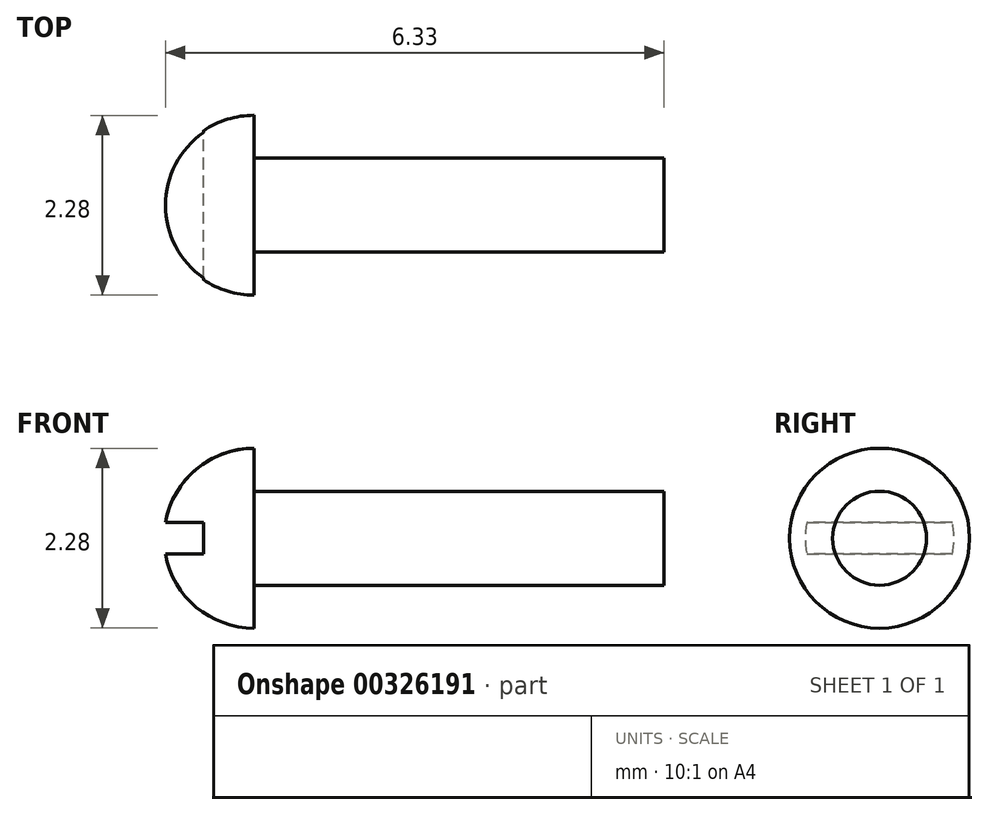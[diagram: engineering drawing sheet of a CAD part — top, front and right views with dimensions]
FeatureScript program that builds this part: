
annotation { "Feature Type Name" : "Feature", "Feature Type Description" : "" }
export const myFeature = defineFeature(function(context is Context, id is Id, definition is map)
    precondition{}
    {
        {
            var Q0;
            Q0=qCreatedBy(makeId("Front.planeOp"),FACE);
            var sketch = newSketch(context, id + "F0", { "sketchPlane" : qUnion([Q0])});
            skLineSegment(sketch, "E0", {"start": v(0, 0) * mm, "end": v(6.35, 0) * mm, "construction": true});
            skLineSegment(sketch, "E1", {"start": v(6.35, 0) * mm, "end": v(6.35, 0.6) * mm});
            skLineSegment(sketch, "E2", {"start": v(6.35, 0.6) * mm, "end": v(1.14, 0.6) * mm});
            skLineSegment(sketch, "E3", {"start": v(1.14, 0.6) * mm, "end": v(1.14, 1.14) * mm});
            skArc(sketch, "E4", {"start": v(1.14, 1.14) * mm, "mid": v(0.33, 0.8) * mm, "end": v(0, 0) * mm});
            skLineSegment(sketch, "E5", {"start": v(0, 0) * mm, "end": v(0, 1.82) * mm, "construction": true});
            skLineSegment(sketch, "E6", {"start": v(0, 0) * mm, "end": v(6.35, 0) * mm});
            skSolve(sketch);
        }
        {
            var Q0;
            Q0=makeQuery(id+"F0.imprint","IMPRINT",FACE,{"disambiguationData":[TD([[makeQuery(id+"F0.imprint","IMPRINT",EDGE,{"derivedFrom":sQuery(id+"F0.wireOp",EDGE,"E1")}),1.0]])]});
            var Q1;
            Q1=sQuery(id+"F0.wireOp",EDGE,"E6");
            revolve(context, id + "F1", {"entities" : qUnion([Q0]), "axis" : qUnion([Q1]), "revolveType" : RevolveType.FULL});
        }
        {
            var Q0;
            Q0=qCreatedBy(makeId("Front.planeOp"),FACE);
            var sketch = newSketch(context, id + "F2", { "sketchPlane" : qUnion([Q0])});
            skLineSegment(sketch, "E7.bottom", {"start": v(0, 0.2) * mm, "end": v(0.5, 0.2) * mm});
            skLineSegment(sketch, "E7.top", {"start": v(0, -0.2) * mm, "end": v(0.5, -0.2) * mm});
            skLineSegment(sketch, "E7.left", {"start": v(0, 0.2) * mm, "end": v(0, -0.2) * mm});
            skLineSegment(sketch, "E7.right", {"start": v(0.5, 0.2) * mm, "end": v(0.5, -0.2) * mm});
            skSolve(sketch);
        }
        {
            var Q0;
            Q0 = qSketchRegion(id + "F2", true);
            extrude(context, id + "F3", {"entities" : qUnion([Q0]), "operationType" : NewBodyOperationType.REMOVE, "depth" : 25 * mm, "symmetric" : true});
        }
    });
